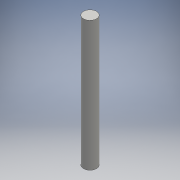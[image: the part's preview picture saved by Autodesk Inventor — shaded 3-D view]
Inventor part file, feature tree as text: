
AUTODESK INVENTOR PART (.ipt)
format: ipt  version: 2016 (Build 200138000, 138)  size: 84,480 bytes
history: native  units: mm
features: extrude x1, sketch x1
ambient origin geometry x8: Origin, YZ Plane, XZ Plane, XY Plane, X Axis, Y Axis, Z Axis, Center Point
bodies: Solid1 (feature_tree)
feature tree (2):
  extrude  "Extrusion1"  Depth=300.0mm TaperAngle=0.0deg
  sketch  "Sketch1"  dims[d0=30.0mm d1=300.0mm d2=0.0mm]
